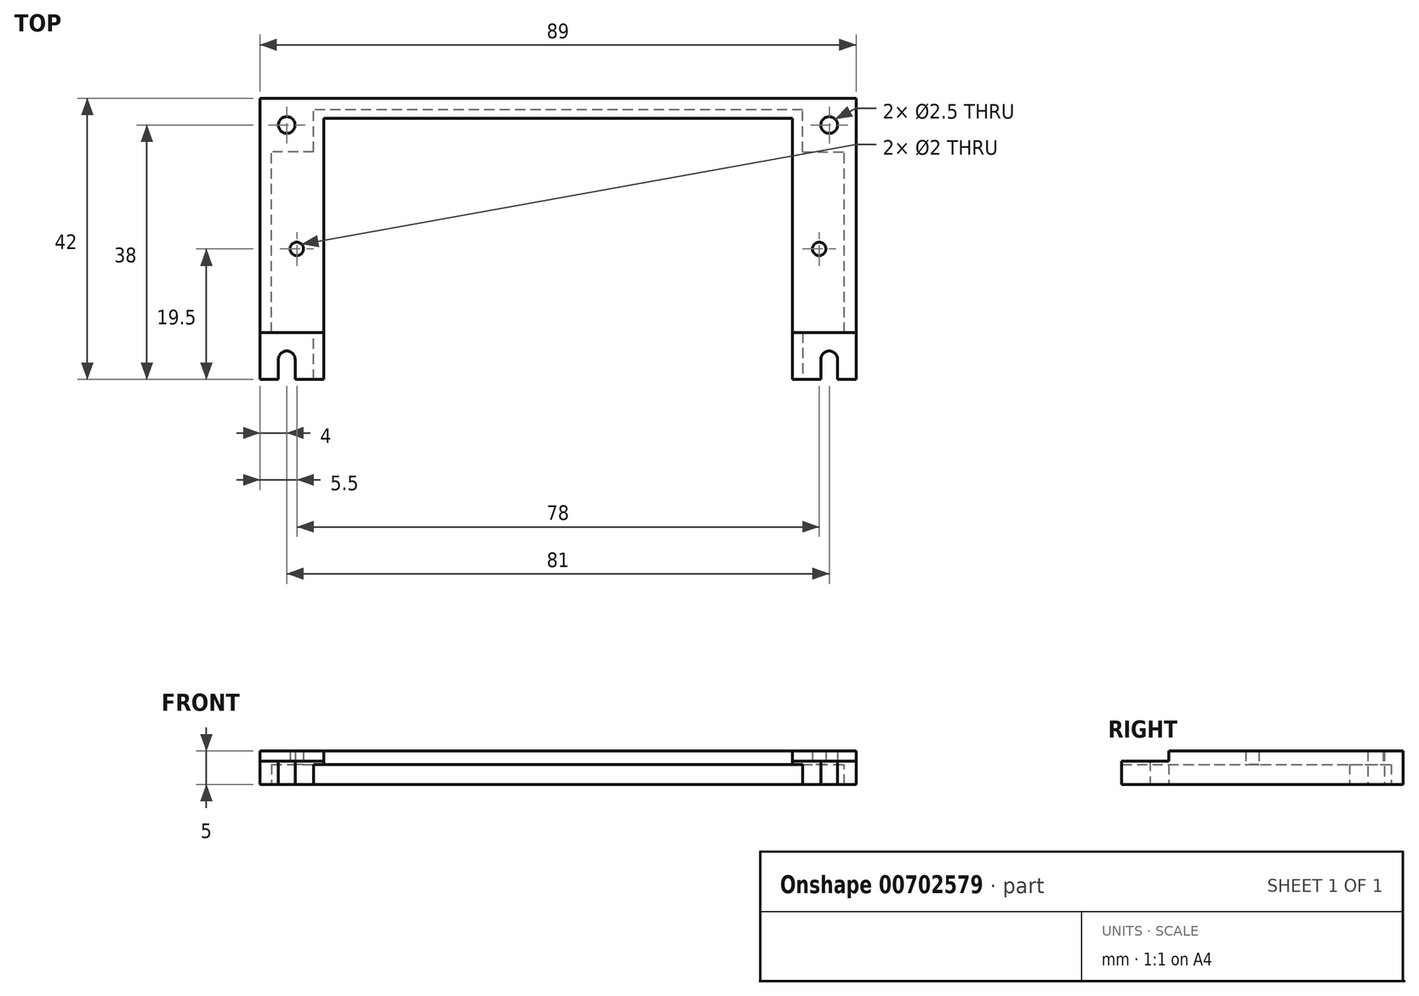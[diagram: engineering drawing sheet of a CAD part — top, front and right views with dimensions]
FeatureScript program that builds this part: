
annotation { "Feature Type Name" : "Feature", "Feature Type Description" : "" }
export const myFeature = defineFeature(function(context is Context, id is Id, definition is map)
    precondition{}
    {
        {
            var Q0;
            Q0=qCreatedBy(makeId("Top.planeOp"),FACE);
            var sketch = newSketch(context, id + "F0", { "sketchPlane" : qUnion([Q0])});
            skLineSegment(sketch, "E0.bottom", {"start": v(44.5, -22.5) * mm, "end": v(-44.5, -22.5) * mm});
            skLineSegment(sketch, "E0.top", {"start": v(44.5, 22.5) * mm, "end": v(-44.5, 22.5) * mm});
            skLineSegment(sketch, "E0.left", {"start": v(44.5, -22.5) * mm, "end": v(44.5, 22.5) * mm});
            skLineSegment(sketch, "E0.right", {"start": v(-44.5, -22.5) * mm, "end": v(-44.5, 22.5) * mm});
            skPoint(sketch, "E0.middle", {"position": v(0, 0) * mm});
            skSolve(sketch);
        }
        {
            var Q0;
            Q0=qSketchRegion(id+"F0",true);
            extrude(context, id + "F1", {"entities" : qUnion([Q0]), "depth" : 5 * mm, "offsetDistance" : 25 * mm});
        }
        {
            var Q0;
            Q0=qCreatedBy(makeId("Top.planeOp"),FACE);
            var sketch = newSketch(context, id + "F2", { "sketchPlane" : qUnion([Q0])});
            skLineSegment(sketch, "E1.bottom", {"start": v(35, -19.5) * mm, "end": v(-35, -19.5) * mm});
            skLineSegment(sketch, "E1.top", {"start": v(35, 19.5) * mm, "end": v(-35, 19.5) * mm});
            skLineSegment(sketch, "E1.left", {"start": v(35, -19.5) * mm, "end": v(35, 19.5) * mm});
            skLineSegment(sketch, "E1.right", {"start": v(-35, -19.5) * mm, "end": v(-35, 19.5) * mm});
            skPoint(sketch, "E1.middle", {"position": v(0, 0) * mm});
            skSolve(sketch);
        }
        {
            var Q0;
            Q0=qSketchRegion(id+"F2",true);
            extrude(context, id + "F3", {"entities" : qUnion([Q0]), "operationType" : NewBodyOperationType.REMOVE, "depth" : 25 * mm, "offsetDistance" : 25 * mm});
        }
        {
            var Q0;
            Q0=qCreatedBy(makeId("Top.planeOp"),FACE);
            var sketch = newSketch(context, id + "F4", { "sketchPlane" : qUnion([Q0])});
            skLineSegment(sketch, "E2.bottom", {"start": v(42.75, -20.75) * mm, "end": v(-42.75, -20.75) * mm});
            skLineSegment(sketch, "E2.top", {"start": v(42.75, 20.75) * mm, "end": v(-42.75, 20.75) * mm});
            skLineSegment(sketch, "E2.left", {"start": v(42.75, -20.75) * mm, "end": v(42.75, 20.75) * mm});
            skLineSegment(sketch, "E2.right", {"start": v(-42.75, -20.75) * mm, "end": v(-42.75, 20.75) * mm});
            skPoint(sketch, "E2.middle", {"position": v(0, 0) * mm});
            skSolve(sketch);
        }
        {
            var Q0;
            Q0=qSketchRegion(id+"F4",true);
            extrude(context, id + "F5", {"entities" : qUnion([Q0]), "operationType" : NewBodyOperationType.REMOVE, "depth" : 3 * mm, "offsetDistance" : 25 * mm});
        }
        {
            var Q0;
            Q0=qCreatedBy(makeId("Top.planeOp"),FACE);
            var sketch = newSketch(context, id + "F6", { "sketchPlane" : qUnion([Q0])});
            skLineSegment(sketch, "E3.bottom", {"start": v(-36.5, 14.5) * mm, "end": v(-44.5, 14.5) * mm});
            skLineSegment(sketch, "E3.top", {"start": v(-36.5, 22.5) * mm, "end": v(-44.5, 22.5) * mm});
            skLineSegment(sketch, "E3.left", {"start": v(-36.5, 14.5) * mm, "end": v(-36.5, 22.5) * mm});
            skLineSegment(sketch, "E3.right", {"start": v(-44.5, 14.5) * mm, "end": v(-44.5, 22.5) * mm});
            skPoint(sketch, "E3.middle", {"position": v(-40.5, 18.5) * mm});
            skLineSegment(sketch, "E4.bottom", {"start": v(-44.5, -22.5) * mm, "end": v(-36.5, -22.5) * mm});
            skLineSegment(sketch, "E4.top", {"start": v(-44.5, -12.5) * mm, "end": v(-36.5, -12.5) * mm});
            skLineSegment(sketch, "E4.left", {"start": v(-44.5, -22.5) * mm, "end": v(-44.5, -12.5) * mm});
            skLineSegment(sketch, "E4.right", {"start": v(-36.5, -22.5) * mm, "end": v(-36.5, -12.5) * mm});
            skPoint(sketch, "E4.middle", {"position": v(-40.5, -17.5) * mm});
            skLineSegment(sketch, "E5.bottom", {"start": v(36.5, 14.5) * mm, "end": v(44.5, 14.5) * mm});
            skLineSegment(sketch, "E5.top", {"start": v(36.5, 22.5) * mm, "end": v(44.5, 22.5) * mm});
            skLineSegment(sketch, "E5.left", {"start": v(36.5, 14.5) * mm, "end": v(36.5, 22.5) * mm});
            skLineSegment(sketch, "E5.right", {"start": v(44.5, 14.5) * mm, "end": v(44.5, 22.5) * mm});
            skPoint(sketch, "E5.middle", {"position": v(40.5, 18.5) * mm});
            skLineSegment(sketch, "E6.bottom", {"start": v(44.5, -12.5) * mm, "end": v(36.5, -12.5) * mm});
            skLineSegment(sketch, "E6.top", {"start": v(44.5, -22.5) * mm, "end": v(36.5, -22.5) * mm});
            skLineSegment(sketch, "E6.left", {"start": v(44.5, -12.5) * mm, "end": v(44.5, -22.5) * mm});
            skLineSegment(sketch, "E6.right", {"start": v(36.5, -12.5) * mm, "end": v(36.5, -22.5) * mm});
            skSolve(sketch);
        }
        {
            var Q0;
            Q0=qSketchRegion(id+"F6",true);
            extrude(context, id + "F7", {"entities" : qUnion([Q0]), "operationType" : NewBodyOperationType.ADD, "depth" : 3 * mm, "offsetDistance" : 25 * mm});
        }
        {
            var Q0;
            Q0=qCreatedBy(makeId("Top.planeOp"),FACE);
            var sketch = newSketch(context, id + "F8", { "sketchPlane" : qUnion([Q0])});
            skCircle(sketch, "E7", {"center": v(40.5, -18.5) * mm, "radius": 1.25 * mm});
            skCircle(sketch, "E8", {"center": v(40.5, 18.5) * mm, "radius": 1.25 * mm});
            skCircle(sketch, "E9", {"center": v(-40.5, -18.5) * mm, "radius": 1.25 * mm});
            skCircle(sketch, "E10", {"center": v(-40.5, 18.5) * mm, "radius": 1.25 * mm});
            skCircle(sketch, "E11", {"center": v(-39, 0) * mm, "radius": 1 * mm});
            skCircle(sketch, "E12", {"center": v(39, 0) * mm, "radius": 1 * mm});
            skCircle(sketch, "E13.1.0.0", {"center": v(-40.5, -16.5) * mm, "radius": 1.25 * mm});
            skLineSegment(sketch, "E13.direction1", {"start": v(-40.5, -18.5) * mm, "end": v(-40.5, -16.5) * mm, "construction": true});
            skLineSegment(sketch, "E14", {"start": v(-39.25, -16.5) * mm, "end": v(-39.25, -18.5) * mm});
            skLineSegment(sketch, "E15", {"start": v(-41.75, -16.5) * mm, "end": v(-41.75, -18.5) * mm});
            skCircle(sketch, "E16.1.0.0", {"center": v(40.5, -16.5) * mm, "radius": 1.25 * mm});
            skLineSegment(sketch, "E16.direction1", {"start": v(40.5, -18.5) * mm, "end": v(40.5, -16.5) * mm, "construction": true});
            skLineSegment(sketch, "E17", {"start": v(39.25, -16.5) * mm, "end": v(39.25, -18.5) * mm});
            skLineSegment(sketch, "E18", {"start": v(41.75, -16.5) * mm, "end": v(41.75, -18.5) * mm});
            skSolve(sketch);
        }
        {
            var Q0;
            Q0=qSketchRegion(id+"F8",true);
            extrude(context, id + "F9", {"entities" : qUnion([Q0]), "operationType" : NewBodyOperationType.REMOVE, "depth" : 25 * mm, "offsetDistance" : 25 * mm});
        }
        {
            var Q0;
            Q0=makeQuery(id+"F1.opExtrude","CAP_FACE",FACE,{"disambiguationData":[OSD([sQuery(id+"F0.wireOp",EDGE,"E0.bottom"),sQuery(id+"F0.wireOp",EDGE,"E0.top"),sQuery(id+"F0.wireOp",EDGE,"E0.left"),sQuery(id+"F0.wireOp",EDGE,"E0.right")])],"isStart":false});
            var sketch = newSketch(context, id + "F10", { "sketchPlane" : qUnion([Q0])});
            skLineSegment(sketch, "E19.bottom", {"start": v(-44.5, -22.5) * mm, "end": v(-35, -22.5) * mm});
            skLineSegment(sketch, "E19.top", {"start": v(-44.5, -12.5) * mm, "end": v(-35, -12.5) * mm});
            skLineSegment(sketch, "E19.left", {"start": v(-44.5, -22.5) * mm, "end": v(-44.5, -12.5) * mm});
            skLineSegment(sketch, "E19.right", {"start": v(-35, -22.5) * mm, "end": v(-35, -12.5) * mm});
            skLineSegment(sketch, "E20.bottom", {"start": v(44.5, -22.5) * mm, "end": v(35, -22.5) * mm});
            skLineSegment(sketch, "E20.top", {"start": v(44.5, -12.5) * mm, "end": v(35, -12.5) * mm});
            skLineSegment(sketch, "E20.left", {"start": v(44.5, -22.5) * mm, "end": v(44.5, -12.5) * mm});
            skLineSegment(sketch, "E20.right", {"start": v(35, -22.5) * mm, "end": v(35, -12.5) * mm});
            skLineSegment(sketch, "E21.bottom", {"start": v(-35, -22.5) * mm, "end": v(35, -22.5) * mm});
            skLineSegment(sketch, "E21.top", {"start": v(-35, -19.5) * mm, "end": v(35, -19.5) * mm});
            skLineSegment(sketch, "E21.left", {"start": v(-35, -22.5) * mm, "end": v(-35, -19.5) * mm});
            skLineSegment(sketch, "E21.right", {"start": v(35, -22.5) * mm, "end": v(35, -19.5) * mm});
            skSolve(sketch);
        }
        {
            var Q0;
            Q0 = qSketchRegion(id + "F10", true);
            extrude(context, id + "F11", {"entities" : qUnion([Q0]), "operationType" : NewBodyOperationType.REMOVE, "oppositeDirection" : true, "depth" : 1.5 * mm, "offsetDistance" : 25 * mm});
        }
        {
            var Q0;
            {var subQ7=sQuery(id+"F10.wireOp",EDGE,"E20.top");var subQ8=sQuery(id+"F10.wireOp",EDGE,"E19.top");Q0=makeQuery(id+"F11.boolean.opBoolean","COPY",FACE,{"disambiguationData":[TD([makeQuery(id+"F1.opExtrude","SWEPT_FACE",FACE,{"disambiguationData":[OSD([sQuery(id+"F0.wireOp",EDGE,"E0.bottom")])]})])],"derivedFrom":makeQuery(id+"F11.opExtrude","CAP_FACE",FACE,{"disambiguationData":[OSD([sQuery(id+"F10.wireOp",EDGE,"E19.bottom"),subQ8,sQuery(id+"F10.wireOp",EDGE,"E19.left"),sQuery(id+"F10.wireOp",EDGE,"E19.right"),sQuery(id+"F10.wireOp",EDGE,"E20.bottom"),subQ7,sQuery(id+"F10.wireOp",EDGE,"E20.left"),sQuery(id+"F10.wireOp",EDGE,"E20.right"),sQuery(id+"F10.wireOp",EDGE,"E21.bottom"),sQuery(id+"F10.wireOp",EDGE,"E21.top")])],"isStart":false})});}
            var sketch = newSketch(context, id + "F12", { "sketchPlane" : qUnion([Q0])});
            skLineSegment(sketch, "E22.bottom", {"start": v(41.75, -16.5) * mm, "end": v(39.25, -16.5) * mm});
            skLineSegment(sketch, "E22.top", {"start": v(41.75, -26.14) * mm, "end": v(39.25, -26.14) * mm});
            skLineSegment(sketch, "E22.left", {"start": v(41.75, -16.5) * mm, "end": v(41.75, -26.14) * mm});
            skLineSegment(sketch, "E22.right", {"start": v(39.25, -16.5) * mm, "end": v(39.25, -26.14) * mm});
            skLineSegment(sketch, "E23.bottom", {"start": v(-39.25, -16.5) * mm, "end": v(-41.75, -16.5) * mm});
            skLineSegment(sketch, "E23.top", {"start": v(-39.25, -24.9) * mm, "end": v(-41.75, -24.9) * mm});
            skLineSegment(sketch, "E23.left", {"start": v(-39.25, -16.5) * mm, "end": v(-39.25, -24.9) * mm});
            skLineSegment(sketch, "E23.right", {"start": v(-41.75, -16.5) * mm, "end": v(-41.75, -24.9) * mm});
            skSolve(sketch);
        }
        {
            var Q0;
            Q0 = qSketchRegion(id + "F12", true);
            extrude(context, id + "F13", {"entities" : qUnion([Q0]), "operationType" : NewBodyOperationType.REMOVE, "oppositeDirection" : true, "depth" : 25 * mm, "offsetDistance" : 25 * mm});
        }
        {
            var Q0;
            {var subQ2=sQuery(id+"F0.wireOp",EDGE,"E0.bottom");var subQ5=sQuery(id+"F8.wireOp",EDGE,"E14");var subQ6=makeQuery(id+"F9.boolean.opBoolean","COPY",FACE,{"derivedFrom":makeQuery(id+"F9.opExtrude","SWEPT_FACE",FACE,{"disambiguationData":[OSD([subQ5])]})});var subQ13=makeQuery(id+"F1.opExtrude","SWEPT_FACE",FACE,{"disambiguationData":[OSD([subQ2])]});Q0=makeQuery(id+"F13.boolean.opBoolean","SPLIT",FACE,{"disambiguationData":[TD([subQ6])],"derivedFrom":subQ13});}
            var sketch = newSketch(context, id + "F14", { "sketchPlane" : qUnion([Q0])});
            skLineSegment(sketch, "E24.bottom", {"start": v(-44.5, 3.5) * mm, "end": v(65.5, 3.5) * mm});
            skLineSegment(sketch, "E24.top", {"start": v(-44.5, 0) * mm, "end": v(65.5, 0) * mm});
            skLineSegment(sketch, "E24.left", {"start": v(-44.5, 3.5) * mm, "end": v(-44.5, 0) * mm});
            skLineSegment(sketch, "E24.right", {"start": v(65.5, 3.5) * mm, "end": v(65.5, 0) * mm});
            skSolve(sketch);
        }
        {
            var Q0;
            Q0 = qSketchRegion(id + "F14", true);
            extrude(context, id + "F15", {"entities" : qUnion([Q0]), "operationType" : NewBodyOperationType.REMOVE, "oppositeDirection" : true, "depth" : 3 * mm, "offsetDistance" : 25 * mm});
        }
    });
